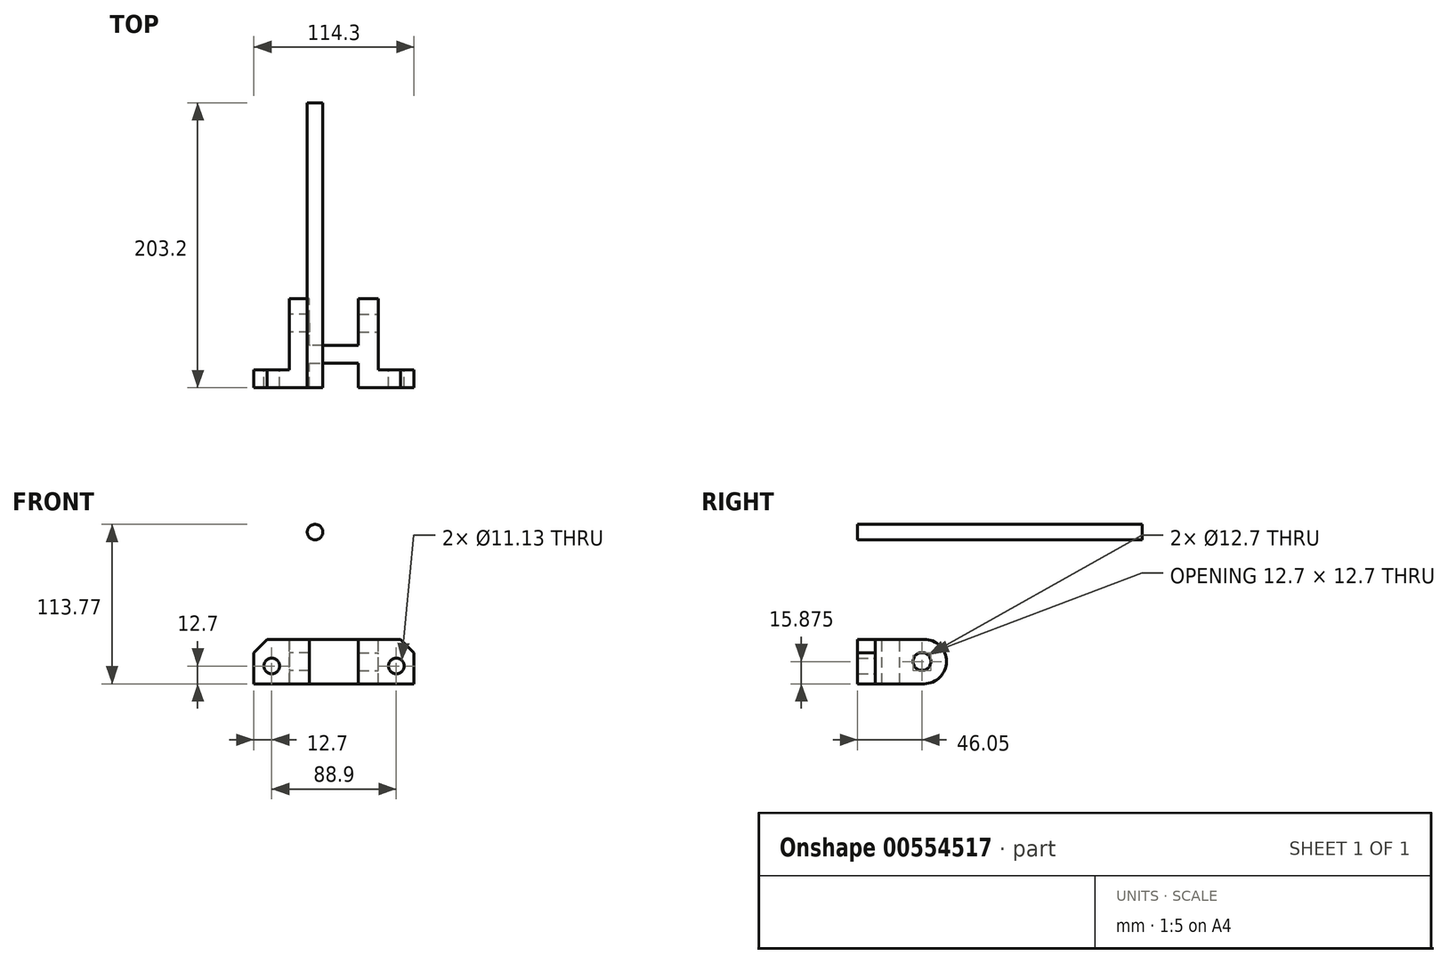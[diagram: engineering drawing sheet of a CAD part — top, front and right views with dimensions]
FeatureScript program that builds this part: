
annotation { "Feature Type Name" : "Feature", "Feature Type Description" : "" }
export const myFeature = defineFeature(function(context is Context, id is Id, definition is map)
    precondition{}
    {
        {
            var Q0;
            Q0=qCreatedBy(makeId("Top.planeOp"),FACE);
            var sketch = newSketch(context, id + "F0", { "sketchPlane" : qUnion([Q0])});
            skLineSegment(sketch, "E0", {"start": v(0, 0) * mm, "end": v(39.7, 0) * mm});
            skLineSegment(sketch, "E1", {"start": v(39.7, 0) * mm, "end": v(39.7, 12.7) * mm});
            skLineSegment(sketch, "E2", {"start": v(39.7, 12.7) * mm, "end": v(14.3, 12.7) * mm});
            skLineSegment(sketch, "E3", {"start": v(14.3, 12.7) * mm, "end": v(14.3, 63.5) * mm});
            skLineSegment(sketch, "E4", {"start": v(14.3, 63.5) * mm, "end": v(0.03, 63.5) * mm});
            skLineSegment(sketch, "E5", {"start": v(0.03, 63.5) * mm, "end": v(0.03, 30.18) * mm});
            skLineSegment(sketch, "E6", {"start": v(0.03, 30.18) * mm, "end": v(-34.93, 30.18) * mm});
            skLineSegment(sketch, "E7", {"start": v(-34.93, 30.18) * mm, "end": v(-34.93, 63.5) * mm});
            skLineSegment(sketch, "E8", {"start": v(-34.93, 63.5) * mm, "end": v(-49.2, 63.5) * mm});
            skLineSegment(sketch, "E9", {"start": v(-49.2, 63.5) * mm, "end": v(-49.2, 12.7) * mm});
            skLineSegment(sketch, "E10", {"start": v(-49.2, 12.7) * mm, "end": v(-74.6, 12.7) * mm});
            skLineSegment(sketch, "E11", {"start": v(-74.6, 12.7) * mm, "end": v(-74.6, 0) * mm});
            skLineSegment(sketch, "E12", {"start": v(-74.6, 0) * mm, "end": v(-34.93, 0) * mm});
            skLineSegment(sketch, "E13", {"start": v(-34.93, 0) * mm, "end": v(-34.93, 17.48) * mm});
            skLineSegment(sketch, "E14", {"start": v(-34.93, 17.48) * mm, "end": v(0, 17.48) * mm});
            skLineSegment(sketch, "E15", {"start": v(0, 17.48) * mm, "end": v(0, 0) * mm});
            skSolve(sketch);
        }
        {
            var Q0;
            Q0=makeQuery(id+"F0.imprint","IMPRINT",FACE,{"disambiguationData":[TD([[makeQuery(id+"F0.imprint","IMPRINT",EDGE,{"derivedFrom":sQuery(id+"F0.wireOp",EDGE,"E0")}),1.0]])]});
            extrude(context, id + "F1", {"entities" : qUnion([Q0]), "oppositeDirection" : true, "depth" : 31.75 * mm, "offsetDistance" : 25.4 * mm});
        }
        {
            var Q0;
            Q0=makeQuery(id+"F1.opExtrude","SWEPT_FACE",FACE,{"disambiguationData":[OSD([sQuery(id+"F0.wireOp",EDGE,"E3")])]});
            var sketch = newSketch(context, id + "F2", { "sketchPlane" : qUnion([Q0])});
            skCircle(sketch, "E16", {"center": v(46.05, -15.88) * mm, "radius": 6.35 * mm});
            skSolve(sketch);
        }
        {
            var Q0;
            Q0=makeQuery(id+"F2.imprint","IMPRINT",FACE,{"disambiguationData":[TD([[makeQuery(id+"F2.imprint","IMPRINT",EDGE,{"derivedFrom":sQuery(id+"F2.wireOp",EDGE,"E16")}),1.0]])]});
            extrude(context, id + "F3", {"entities" : qUnion([Q0]), "operationType" : NewBodyOperationType.REMOVE, "oppositeDirection" : true, "depth" : 25.4 * mm, "offsetDistance" : 25.4 * mm});
        }
        {
            var Q0;
            Q0=makeQuery(id+"F1.opExtrude","SWEPT_FACE",FACE,{"disambiguationData":[OSD([sQuery(id+"F0.wireOp",EDGE,"E9")])]});
            var sketch = newSketch(context, id + "F4", { "sketchPlane" : qUnion([Q0])});
            skCircle(sketch, "E17", {"center": v(-46.05, -15.88) * mm, "radius": 6.35 * mm});
            skSolve(sketch);
        }
        {
            var Q0;
            Q0 = qSketchRegion(id + "F4", true);
            extrude(context, id + "F5", {"entities" : qUnion([Q0]), "operationType" : NewBodyOperationType.REMOVE, "oppositeDirection" : true, "depth" : 25.4 * mm, "offsetDistance" : 25.4 * mm});
        }
        {
            var Q0;
            Q0=makeQuery(id+"F1.opExtrude","SWEPT_FACE",FACE,{"disambiguationData":[OSD([sQuery(id+"F0.wireOp",EDGE,"E10")])]});
            var sketch = newSketch(context, id + "F6", { "sketchPlane" : qUnion([Q0])});
            skCircle(sketch, "E18", {"center": v(61.9, -19.05) * mm, "radius": 5.56 * mm});
            skCircle(sketch, "E19", {"center": v(-27, -19.05) * mm, "radius": 5.56 * mm});
            skSolve(sketch);
        }
        {
            var Q0;
            Q0 = qSketchRegion(id + "F6", true);
            extrude(context, id + "F7", {"entities" : qUnion([Q0]), "operationType" : NewBodyOperationType.REMOVE, "oppositeDirection" : true, "depth" : 25.4 * mm, "offsetDistance" : 25.4 * mm});
        }
        {
            var Q0;
            Q0=makeQuery(id+"F1.opExtrude","CAP_EDGE",EDGE,{"disambiguationData":[OSD([sQuery(id+"F0.wireOp",EDGE,"E11")])],"isStart":true});
            var Q1;
            Q1=makeQuery(id+"F1.opExtrude","CAP_EDGE",EDGE,{"disambiguationData":[OSD([sQuery(id+"F0.wireOp",EDGE,"E1")])],"isStart":true});
            chamfer(context, id + "F8", {"entities" : qUnion([Q0, Q1]), "width" : 9.52 * mm, "tangentPropagation" : true});
        }
        {
            var Q0;
            Q0=makeQuery(id+"F1.opExtrude","CAP_EDGE",EDGE,{"disambiguationData":[OSD([sQuery(id+"F0.wireOp",EDGE,"E8")])],"isStart":true});
            var Q1;
            Q1=makeQuery(id+"F1.opExtrude","CAP_EDGE",EDGE,{"disambiguationData":[OSD([sQuery(id+"F0.wireOp",EDGE,"E8")])],"isStart":false});
            var Q2;
            Q2=makeQuery(id+"F1.opExtrude","CAP_EDGE",EDGE,{"disambiguationData":[OSD([sQuery(id+"F0.wireOp",EDGE,"E4")])],"isStart":false});
            var Q3;
            Q3=makeQuery(id+"F1.opExtrude","CAP_EDGE",EDGE,{"disambiguationData":[OSD([sQuery(id+"F0.wireOp",EDGE,"E4")])],"isStart":true});
            fillet(context, id + "F9", {"entities" : qUnion([Q0, Q1, Q2, Q3]), "radius" : 15.88 * mm, "tangentPropagation" : true, "allowEdgeOverflow" : false});
        }
        {
            var Q0;
            Q0=qCreatedBy(makeId("Front.planeOp"),FACE);
            var sketch = newSketch(context, id + "F10", { "sketchPlane" : qUnion([Q0])});
            skCircle(sketch, "E20", {"center": v(-30.96, 76.46) * mm, "radius": 5.56 * mm});
            skSolve(sketch);
        }
        {
            var Q0;
            Q0 = qSketchRegion(id + "F10", true);
            var Q1;
            Q1=makeQuery(id+"F10.imprint","IMPRINT",FACE,{"disambiguationData":[TD([[makeQuery(id+"F10.imprint","IMPRINT",EDGE,{"derivedFrom":sQuery(id+"F10.wireOp",EDGE,"E20")}),1.0]])]});
            extrude(context, id + "F11", {"entities" : qUnion([Q0, Q1]), "oppositeDirection" : true, "depth" : 203.2 * mm, "offsetDistance" : 25.4 * mm});
        }
        {
            var Q0;
            Q0=makeQuery(id+"F1.opExtrude","CAP_FACE",FACE,{"disambiguationData":[OSD([sQuery(id+"F0.wireOp",EDGE,"E0"),sQuery(id+"F0.wireOp",EDGE,"E1"),sQuery(id+"F0.wireOp",EDGE,"E2"),sQuery(id+"F0.wireOp",EDGE,"E3"),sQuery(id+"F0.wireOp",EDGE,"E4"),sQuery(id+"F0.wireOp",EDGE,"E5"),sQuery(id+"F0.wireOp",EDGE,"E6"),sQuery(id+"F0.wireOp",EDGE,"E7"),sQuery(id+"F0.wireOp",EDGE,"E8"),sQuery(id+"F0.wireOp",EDGE,"E9"),sQuery(id+"F0.wireOp",EDGE,"E10"),sQuery(id+"F0.wireOp",EDGE,"E11"),sQuery(id+"F0.wireOp",EDGE,"E12"),sQuery(id+"F0.wireOp",EDGE,"E13"),sQuery(id+"F0.wireOp",EDGE,"E14"),sQuery(id+"F0.wireOp",EDGE,"E15")])],"isStart":true});
            var sketch = newSketch(context, id + "F12", { "sketchPlane" : qUnion([Q0])});
            skCircle(sketch, "E21", {"center": v(120.37, 66.8) * mm, "radius": 41.56 * mm});
            skSolve(sketch);
        }
    });
